# Revit family: 700_OXXO_Custom
name_source: partatom
category: Doors
revit_build: Autodesk Revit 2014 (Build: 20130308_1515(x64)
units: mm (PartAtom-declared; Revit-internal decimal feet)

## types (1)
- OXXO_Custom
    Default Sill Height = 0 mm  [stored 0 ft]
    Description = Sliding door, OXXO custom
    Frame Thickness = 72 mm
    Limit Door Height Max = 2142 mm
    Limit Door Height Min = 342 mm
    Limit Door Width Min = 1183 mm
    Limit Sash Height Max = 2100 mm
    Limit Sash Height Min = 300 mm  [stored 0.984252 ft]
    Limit Sash Width Max = 1500 mm
    Limit Sash Width Min = 300 mm  [stored 0.984252 ft]
    Manufacturer = Crealco
    Model = Series 700
    Sash Frame Seal = 2 mm  [stored 0.00656168 ft]
    Sash Frame Side Gap = 10 mm  [stored 0.0328084 ft]
    Sash Frame Top Gap = 16 mm  [stored 0.0524934 ft]
    Sash Sliding Frame Seal = 5 mm  [stored 0.0164042 ft]
    URL = http://www.crealco.co.za
    Wall Closure = By host

note: [stored X ft] marks values corroborated as IEEE doubles in the binary element streams (Revit-internal decimal feet)

## geometry (parser evidence)
native form markers: Sweep x78
no freeform markers — native parametric forms only
